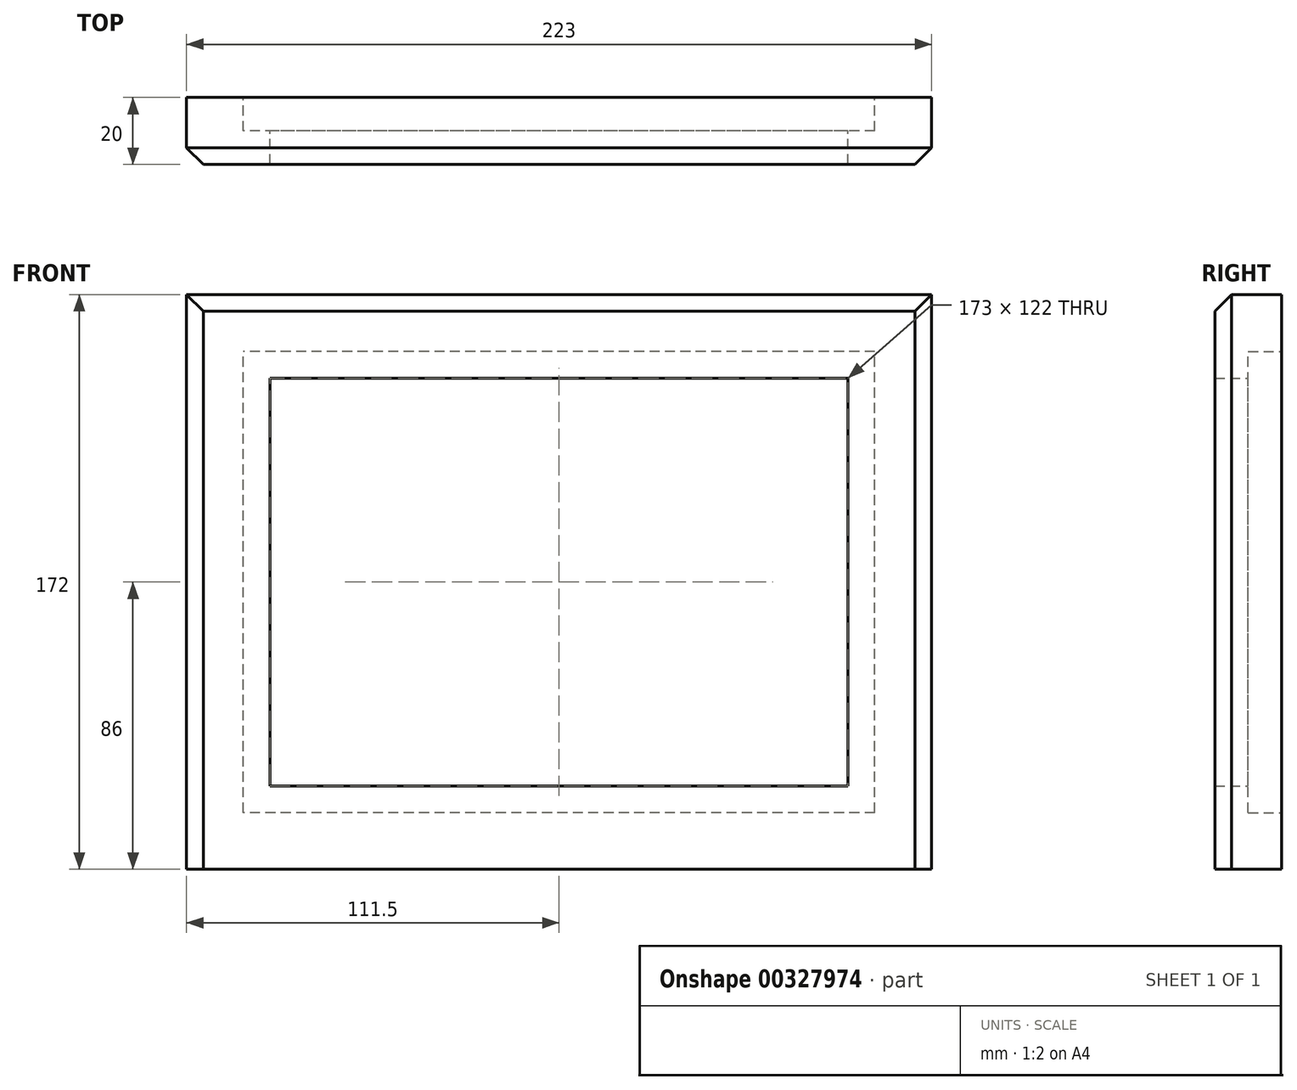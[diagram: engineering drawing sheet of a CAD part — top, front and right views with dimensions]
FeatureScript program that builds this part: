
annotation { "Feature Type Name" : "Feature", "Feature Type Description" : "" }
export const myFeature = defineFeature(function(context is Context, id is Id, definition is map)
    precondition{}
    {
        {
            var Q0;
            Q0=qCreatedBy(makeId("Front.planeOp"),FACE);
            var sketch = newSketch(context, id + "F0", { "sketchPlane" : qUnion([Q0])});
            skLineSegment(sketch, "E0.bottom", {"start": v(86.5, -61) * mm, "end": v(-86.5, -61) * mm});
            skLineSegment(sketch, "E0.top", {"start": v(86.5, 61) * mm, "end": v(-86.5, 61) * mm});
            skLineSegment(sketch, "E0.left", {"start": v(86.5, -61) * mm, "end": v(86.5, 61) * mm});
            skLineSegment(sketch, "E0.right", {"start": v(-86.5, -61) * mm, "end": v(-86.5, 61) * mm});
            skPoint(sketch, "E0.middle", {"position": v(0, 0) * mm});
            skLineSegment(sketch, "E1.bottom", {"start": v(94.5, -69) * mm, "end": v(-94.5, -69) * mm});
            skLineSegment(sketch, "E1.top", {"start": v(94.5, 69) * mm, "end": v(-94.5, 69) * mm});
            skLineSegment(sketch, "E1.left", {"start": v(94.5, -69) * mm, "end": v(94.5, 69) * mm});
            skLineSegment(sketch, "E1.right", {"start": v(-94.5, -69) * mm, "end": v(-94.5, 69) * mm});
            skLineSegment(sketch, "E2.bottom", {"start": v(111.5, -86) * mm, "end": v(-111.5, -86) * mm});
            skLineSegment(sketch, "E2.top", {"start": v(111.5, 86) * mm, "end": v(-111.5, 86) * mm});
            skLineSegment(sketch, "E2.left", {"start": v(111.5, -86) * mm, "end": v(111.5, 86) * mm});
            skLineSegment(sketch, "E2.right", {"start": v(-111.5, -86) * mm, "end": v(-111.5, 86) * mm});
            skLineSegment(sketch, "E3.bottom", {"start": v(-111.5, -86) * mm, "end": v(111.5, -86) * mm});
            skLineSegment(sketch, "E3.top", {"start": v(-111.5, -86) * mm, "end": v(111.5, -86) * mm});
            skLineSegment(sketch, "E3.left", {"start": v(-111.5, -86) * mm, "end": v(-111.5, -86) * mm});
            skLineSegment(sketch, "E3.right", {"start": v(111.5, -86) * mm, "end": v(111.5, -86) * mm});
            skSolve(sketch);
        }
        {
            var Q0;
            Q0=makeQuery(id+"F0.imprint","IMPRINT",FACE,{"disambiguationData":[TD([[makeQuery(id+"F0.imprint","IMPRINT",EDGE,{"derivedFrom":sQuery(id+"F0.wireOp",EDGE,"E1.bottom")}),1.0]])]});
            var Q1;
            Q1=makeQuery(id+"F0.imprint","IMPRINT",FACE,{"disambiguationData":[TD([[makeQuery(id+"F0.imprint","IMPRINT",EDGE,{"derivedFrom":sQuery(id+"F0.wireOp",EDGE,"E3.bottom")}),-1.0]])]});
            var Q2;
            Q2=makeQuery(id+"F0.imprint","IMPRINT",FACE,{"disambiguationData":[TD([[makeQuery(id+"F0.imprint","IMPRINT",EDGE,{"derivedFrom":sQuery(id+"F0.wireOp",EDGE,"E0.bottom")}),1.0]])]});
            extrude(context, id + "F1", {"entities" : qUnion([Q0, Q1, Q2]), "depth" : 20 * mm});
        }
        {
            var Q0;
            Q0=makeQuery(id+"F1.opExtrude","CAP_EDGE",EDGE,{"disambiguationData":[OSD([sQuery(id+"F0.wireOp",EDGE,"E2.right"),sQuery(id+"F0.wireOp",EDGE,"C0Mc5uo2-8IaI-2a1y-d5Gc-MIS5kBU6ZncW.left")])],"isStart":false});
            var Q1;
            Q1=makeQuery(id+"F1.opExtrude","CAP_EDGE",EDGE,{"disambiguationData":[OSD([sQuery(id+"F0.wireOp",EDGE,"E2.top")])],"isStart":false});
            var Q2;
            Q2=makeQuery(id+"F1.opExtrude","CAP_EDGE",EDGE,{"disambiguationData":[OSD([sQuery(id+"F0.wireOp",EDGE,"E2.left"),sQuery(id+"F0.wireOp",EDGE,"C0Mc5uo2-8IaI-2a1y-d5Gc-MIS5kBU6ZncW.right")])],"isStart":false});
            var Q3;
            Q3=makeQuery(id+"F1.opExtrude","CAP_EDGE",EDGE,{"disambiguationData":[OSD([sQuery(id+"F0.wireOp",EDGE,"E3.bottom")])],"isStart":false});
            chamfer(context, id + "F2", {"entities" : qUnion([Q0, Q1, Q2, Q3]), "width" : 5 * mm, "tangentPropagation" : true});
        }
        {
            var Q0;
            Q0=makeQuery(id+"F0.imprint","IMPRINT",FACE,{"disambiguationData":[TD([[makeQuery(id+"F0.imprint","IMPRINT",EDGE,{"derivedFrom":sQuery(id+"F0.wireOp",EDGE,"E0.bottom")}),1.0]])]});
            extrude(context, id + "F3", {"entities" : qUnion([Q0]), "operationType" : NewBodyOperationType.REMOVE, "depth" : 10 * mm});
        }
        {
            var Q0;
            Q0=makeQuery(id+"F1.opExtrude","CAP_FACE",FACE,{"disambiguationData":[OSD([sQuery(id+"F0.wireOp",EDGE,"E0.bottom"),sQuery(id+"F0.wireOp",EDGE,"E0.top"),sQuery(id+"F0.wireOp",EDGE,"E0.left"),sQuery(id+"F0.wireOp",EDGE,"E0.right"),sQuery(id+"F0.wireOp",EDGE,"E2.top"),sQuery(id+"F0.wireOp",EDGE,"E2.left"),sQuery(id+"F0.wireOp",EDGE,"E2.right"),sQuery(id+"F0.wireOp",EDGE,"C0Mc5uo2-8IaI-2a1y-d5Gc-MIS5kBU6ZncW.top"),sQuery(id+"F0.wireOp",EDGE,"C0Mc5uo2-8IaI-2a1y-d5Gc-MIS5kBU6ZncW.left"),sQuery(id+"F0.wireOp",EDGE,"C0Mc5uo2-8IaI-2a1y-d5Gc-MIS5kBU6ZncW.right")])],"isStart":false});
            var sketch = newSketch(context, id + "F4", { "sketchPlane" : qUnion([Q0])});
            skLineSegment(sketch, "E4", {"start": v(-86.5, 61) * mm, "end": v(86.5, -61) * mm, "construction": true});
            skLineSegment(sketch, "E5", {"start": v(-86.5, -61) * mm, "end": v(86.5, 61) * mm, "construction": true});
            skPoint(sketch, "E6", {"position": v(0, 0) * mm});
            skSolve(sketch);
        }
    });
